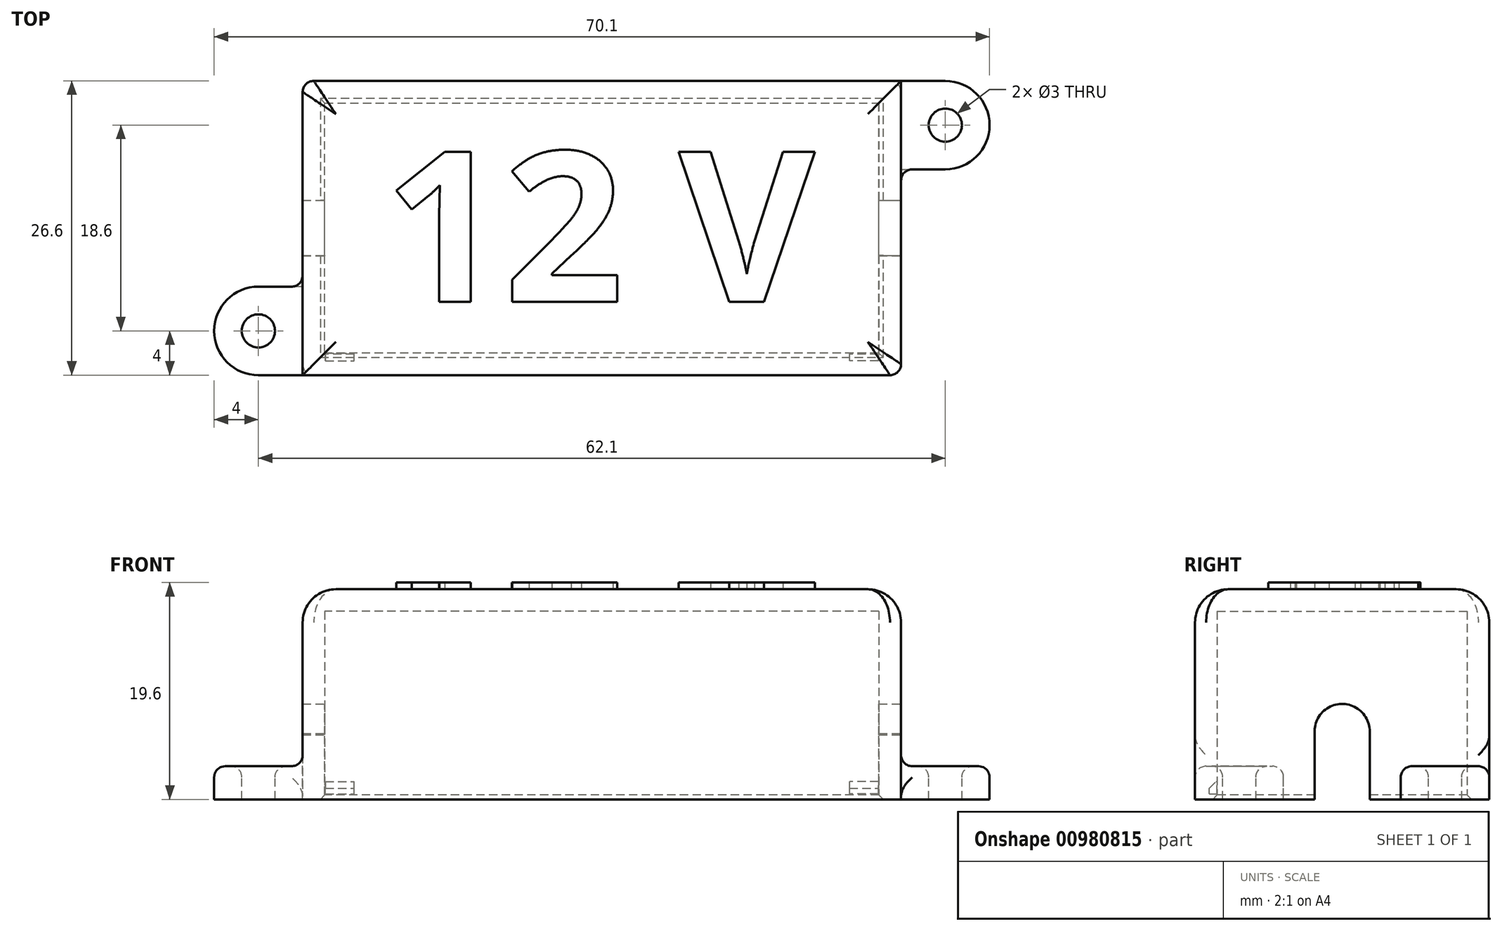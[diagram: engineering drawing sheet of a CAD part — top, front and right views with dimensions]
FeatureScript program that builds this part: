
annotation { "Feature Type Name" : "Feature", "Feature Type Description" : "" }
export const myFeature = defineFeature(function(context is Context, id is Id, definition is map)
    precondition{}
    {
        {
            var Q0;
            Q0=qCreatedBy(makeId("Top.planeOp"),FACE);
            var sketch = newSketch(context, id + "F0", { "sketchPlane" : qUnion([Q0])});
            skLineSegment(sketch, "E0.bottom", {"start": v(25.05, -11.3) * mm, "end": v(-25.05, -11.3) * mm});
            skLineSegment(sketch, "E0.top", {"start": v(25.05, 11.3) * mm, "end": v(-25.05, 11.3) * mm});
            skLineSegment(sketch, "E0.left", {"start": v(25.05, -11.3) * mm, "end": v(25.05, 11.3) * mm});
            skLineSegment(sketch, "E0.right", {"start": v(-25.05, -11.3) * mm, "end": v(-25.05, 11.3) * mm});
            skPoint(sketch, "E0.middle", {"position": v(0, 0) * mm});
            skLineSegment(sketch, "E1.bottom", {"start": v(27.05, -13.3) * mm, "end": v(-27.05, -13.3) * mm});
            skLineSegment(sketch, "E1.top", {"start": v(27.05, 13.3) * mm, "end": v(-27.05, 13.3) * mm});
            skLineSegment(sketch, "E1.left", {"start": v(27.05, -13.3) * mm, "end": v(27.05, 13.3) * mm});
            skLineSegment(sketch, "E1.right", {"start": v(-27.05, -13.3) * mm, "end": v(-27.05, 13.3) * mm});
            skSolve(sketch);
        }
        {
            var Q0;
            Q0 = qSketchRegion(id + "F0", true);
            extrude(context, id + "F1", {"entities" : qUnion([Q0]), "depth" : 17 * mm, "offsetDistance" : 25 * mm});
        }
        {
            var Q0;
            Q0=makeQuery(id+"F1.opExtrude","CAP_FACE",FACE,{"disambiguationData":[OSD([sQuery(id+"F0.wireOp",EDGE,"E0.bottom"),sQuery(id+"F0.wireOp",EDGE,"E0.top"),sQuery(id+"F0.wireOp",EDGE,"E0.left"),sQuery(id+"F0.wireOp",EDGE,"E0.right"),sQuery(id+"F0.wireOp",EDGE,"E1.bottom"),sQuery(id+"F0.wireOp",EDGE,"E1.top"),sQuery(id+"F0.wireOp",EDGE,"E1.left"),sQuery(id+"F0.wireOp",EDGE,"E1.right")])],"isStart":false});
            var sketch = newSketch(context, id + "F2", { "sketchPlane" : qUnion([Q0])});
            skLineSegment(sketch, "E2.0", {"start": v(-27.05, -13.3) * mm, "end": v(-27.05, 13.3) * mm});
            skLineSegment(sketch, "E3.0", {"start": v(27.05, 13.3) * mm, "end": v(-27.05, 13.3) * mm});
            skLineSegment(sketch, "E4.0", {"start": v(27.05, -13.3) * mm, "end": v(27.05, 13.3) * mm});
            skLineSegment(sketch, "E5.0", {"start": v(27.05, -13.3) * mm, "end": v(-27.05, -13.3) * mm});
            skSolve(sketch);
        }
        {
            var Q0;
            Q0 = qSketchRegion(id + "F2", true);
            extrude(context, id + "F3", {"entities" : qUnion([Q0]), "operationType" : NewBodyOperationType.ADD, "depth" : 2 * mm, "offsetDistance" : 25 * mm});
        }
        {
            var Q0;
            Q0=makeQuery(id+"F3.boolean.opBoolean","MERGE",FACE,{"derivedFrom":[makeQuery(id+"F1.opExtrude","SWEPT_FACE",FACE,{"disambiguationData":[OSD([sQuery(id+"F0.wireOp",EDGE,"E1.left")])]}),makeQuery(id+"F3.opExtrude","SWEPT_FACE",FACE,{"disambiguationData":[OSD([sQuery(id+"F2.wireOp",EDGE,"E4.0")])]})]});
            var sketch = newSketch(context, id + "F4", { "sketchPlane" : qUnion([Q0])});
            skLineSegment(sketch, "E6", {"start": v(-2.48, 5.83) * mm, "end": v(-2.48, 0) * mm});
            skLineSegment(sketch, "E7", {"start": v(2.5, 5.96) * mm, "end": v(2.5, 0) * mm});
            skLineSegment(sketch, "E8", {"start": v(2.5, 0) * mm, "end": v(-2.48, 0) * mm});
            skArc(sketch, "E9.trimOffspring", {"start": v(2.5, 5.96) * mm, "mid": v(-0.07, 8.63) * mm, "end": v(-2.48, 5.83) * mm});
            skLineSegment(sketch, "E10.trimOffspring", {"start": v(2.5, 3.63) * mm, "end": v(3.32, 3.63) * mm, "construction": true});
            skPoint(sketch, "E11.start.orphan", {"position": v(0, 3.63) * mm});
            skSolve(sketch);
        }
        {
            var Q0;
            Q0 = qSketchRegion(id + "F4", true);
            extrude(context, id + "F5", {"entities" : qUnion([Q0]), "operationType" : NewBodyOperationType.REMOVE, "endBound" : BoundingType.THROUGH_ALL, "oppositeDirection" : true, "depth" : 25 * mm, "offsetDistance" : 25 * mm});
        }
        {
            var Q0;
            Q0=makeQuery(id+"F3.boolean.opBoolean","MERGE",FACE,{"derivedFrom":[makeQuery(id+"F1.opExtrude","SWEPT_FACE",FACE,{"disambiguationData":[OSD([sQuery(id+"F0.wireOp",EDGE,"E1.left")])]}),makeQuery(id+"F3.opExtrude","SWEPT_FACE",FACE,{"disambiguationData":[OSD([sQuery(id+"F2.wireOp",EDGE,"E4.0")])]})]});
            var sketch = newSketch(context, id + "F6", { "sketchPlane" : qUnion([Q0])});
            skLineSegment(sketch, "E12.bottom", {"start": v(13.3, 0) * mm, "end": v(5.3, 0) * mm});
            skLineSegment(sketch, "E12.top", {"start": v(13.3, 3) * mm, "end": v(5.3, 3) * mm});
            skLineSegment(sketch, "E12.left", {"start": v(13.3, 0) * mm, "end": v(13.3, 3) * mm});
            skLineSegment(sketch, "E12.right", {"start": v(5.3, 0) * mm, "end": v(5.3, 3) * mm});
            skSolve(sketch);
        }
        {
            var Q0;
            Q0 = qSketchRegion(id + "F6", true);
            extrude(context, id + "F7", {"entities" : qUnion([Q0]), "operationType" : NewBodyOperationType.ADD, "depth" : 8 * mm, "offsetDistance" : 25 * mm});
        }
        {
            var Q0;
            Q0=makeQuery(id+"F7.opExtrude","CAP_EDGE",EDGE,{"disambiguationData":[OSD([sQuery(id+"F6.wireOp",EDGE,"E12.right")])],"isStart":false});
            var Q1;
            Q1=makeQuery(id+"F7.opExtrude","CAP_EDGE",EDGE,{"disambiguationData":[OSD([sQuery(id+"F6.wireOp",EDGE,"E12.left")])],"isStart":false});
            fillet(context, id + "F8", {"entities" : qUnion([Q0, Q1]), "radius" : 4 * mm, "tangentPropagation" : true, "allowEdgeOverflow" : false});
        }
        {
            var Q0;
            Q0=makeQuery(id+"F3.boolean.opBoolean","MERGE",FACE,{"derivedFrom":[makeQuery(id+"F1.opExtrude","SWEPT_FACE",FACE,{"disambiguationData":[OSD([sQuery(id+"F0.wireOp",EDGE,"E1.right")])]}),makeQuery(id+"F3.opExtrude","SWEPT_FACE",FACE,{"disambiguationData":[OSD([sQuery(id+"F2.wireOp",EDGE,"E2.0")])]})]});
            var sketch = newSketch(context, id + "F9", { "sketchPlane" : qUnion([Q0])});
            skLineSegment(sketch, "E13.bottom", {"start": v(13.3, 0) * mm, "end": v(5.3, 0) * mm});
            skLineSegment(sketch, "E13.top", {"start": v(13.3, 3) * mm, "end": v(5.3, 3) * mm});
            skLineSegment(sketch, "E13.left", {"start": v(13.3, 0) * mm, "end": v(13.3, 3) * mm});
            skLineSegment(sketch, "E13.right", {"start": v(5.3, 0) * mm, "end": v(5.3, 3) * mm});
            skSolve(sketch);
        }
        {
            var Q0;
            Q0 = qSketchRegion(id + "F9", true);
            extrude(context, id + "F10", {"entities" : qUnion([Q0]), "operationType" : NewBodyOperationType.ADD, "depth" : 8 * mm, "offsetDistance" : 25 * mm});
        }
        {
            var Q0;
            Q0=makeQuery(id+"F10.opExtrude","CAP_EDGE",EDGE,{"disambiguationData":[OSD([sQuery(id+"F9.wireOp",EDGE,"E13.right")])],"isStart":false});
            var Q1;
            Q1=makeQuery(id+"F10.opExtrude","CAP_EDGE",EDGE,{"disambiguationData":[OSD([sQuery(id+"F9.wireOp",EDGE,"E13.left")])],"isStart":false});
            fillet(context, id + "F11", {"entities" : qUnion([Q0, Q1]), "radius" : 4 * mm, "tangentPropagation" : true, "allowEdgeOverflow" : false});
        }
        {
            var Q0;
            Q0=makeQuery(id+"F10.opExtrude","SWEPT_FACE",FACE,{"disambiguationData":[OSD([sQuery(id+"F9.wireOp",EDGE,"E13.top")])]});
            var sketch = newSketch(context, id + "F12", { "sketchPlane" : qUnion([Q0])});
            skLineSegment(sketch, "E14", {"start": v(-31.05, -5.3) * mm, "end": v(-31.05, -13.3) * mm, "construction": true});
            skCircle(sketch, "E15", {"center": v(-31.05, -9.3) * mm, "radius": 1.5 * mm});
            skSolve(sketch);
        }
        {
            var Q0;
            Q0 = qSketchRegion(id + "F12", true);
            extrude(context, id + "F13", {"entities" : qUnion([Q0]), "operationType" : NewBodyOperationType.REMOVE, "oppositeDirection" : true, "depth" : 25 * mm, "offsetDistance" : 25 * mm});
        }
        {
            var Q0;
            Q0=makeQuery(id+"F7.opExtrude","SWEPT_FACE",FACE,{"disambiguationData":[OSD([sQuery(id+"F6.wireOp",EDGE,"E12.top")])]});
            var sketch = newSketch(context, id + "F14", { "sketchPlane" : qUnion([Q0])});
            skLineSegment(sketch, "E16", {"start": v(31.05, 13.3) * mm, "end": v(31.05, 5.3) * mm, "construction": true});
            skCircle(sketch, "E17", {"center": v(31.05, 9.3) * mm, "radius": 1.5 * mm});
            skSolve(sketch);
        }
        {
            var Q0;
            Q0 = qSketchRegion(id + "F14", true);
            extrude(context, id + "F15", {"entities" : qUnion([Q0]), "operationType" : NewBodyOperationType.REMOVE, "oppositeDirection" : true, "depth" : 25 * mm, "offsetDistance" : 25 * mm});
        }
        {
            var Q0;
            Q0=makeQuery(id+"F3.opExtrude","CAP_FACE",FACE,{"disambiguationData":[OSD([sQuery(id+"F2.wireOp",EDGE,"E2.0"),sQuery(id+"F2.wireOp",EDGE,"E3.0"),sQuery(id+"F2.wireOp",EDGE,"E4.0"),sQuery(id+"F2.wireOp",EDGE,"E5.0")])],"isStart":false});
            fillet(context, id + "F16", {"entities" : qUnion([Q0]), "radius" : 3 * mm, "tangentPropagation" : true, "allowEdgeOverflow" : false});
        }
        {
            var Q0;
            Q0=makeQuery(id+"F1.opExtrude","SWEPT_FACE",FACE,{"disambiguationData":[OSD([sQuery(id+"F0.wireOp",EDGE,"E0.bottom")])]});
            var sketch = newSketch(context, id + "F17", { "sketchPlane" : qUnion([Q0])});
            skLineSegment(sketch, "E18", {"start": v(0, 0) * mm, "end": v(0, 17) * mm, "construction": true});
            skLineSegment(sketch, "E19.bottom", {"start": v(25, 0.5) * mm, "end": v(22.4, 0.5) * mm});
            skLineSegment(sketch, "E19.top", {"start": v(25, 1.6) * mm, "end": v(22.4, 1.6) * mm});
            skLineSegment(sketch, "E19.left", {"start": v(25, 0.5) * mm, "end": v(25, 1.6) * mm});
            skLineSegment(sketch, "E19.right", {"start": v(22.4, 0.5) * mm, "end": v(22.4, 1.6) * mm});
            skLineSegment(sketch, "E20.MirrorCS", {"start": v(-25, 1.6) * mm, "end": v(-22.4, 1.6) * mm});
            skLineSegment(sketch, "E21.MirrorCS", {"start": v(-25, 0.5) * mm, "end": v(-22.4, 0.5) * mm});
            skLineSegment(sketch, "E22.MirrorCS", {"start": v(-22.4, 0.5) * mm, "end": v(-22.4, 1.6) * mm});
            skLineSegment(sketch, "E23.MirrorCS", {"start": v(-25, 0.5) * mm, "end": v(-25, 1.6) * mm});
            skSolve(sketch);
        }
        {
            var Q0;
            Q0 = qSketchRegion(id + "F17", true);
            extrude(context, id + "F18", {"entities" : qUnion([Q0]), "operationType" : NewBodyOperationType.REMOVE, "oppositeDirection" : true, "depth" : .7 * mm, "offsetDistance" : 25 * mm});
        }
        {
            var Q0;
            Q0=makeQuery(id+"F18.boolean.opBoolean","COPY",EDGE,{"derivedFrom":makeQuery(id+"F18.opExtrude","CAP_EDGE",EDGE,{"disambiguationData":[OSD([sQuery(id+"F17.wireOp",EDGE,"E20.MirrorCS")])],"isStart":false})});
            var Q1;
            Q1=makeQuery(id+"F18.boolean.opBoolean","COPY",EDGE,{"derivedFrom":makeQuery(id+"F18.opExtrude","CAP_EDGE",EDGE,{"disambiguationData":[OSD([sQuery(id+"F17.wireOp",EDGE,"E19.top")])],"isStart":false})});
            chamfer(context, id + "F19", {"entities" : qUnion([Q0, Q1]), "width" : .6 * mm, "tangentPropagation" : true});
        }
        {
            var Q0;
            Q0=makeQuery(id+"F10.opExtrude","SWEPT_FACE",FACE,{"disambiguationData":[OSD([sQuery(id+"F9.wireOp",EDGE,"E13.top")])]});
            var Q1;
            Q1=makeQuery(id+"F7.opExtrude","SWEPT_FACE",FACE,{"disambiguationData":[OSD([sQuery(id+"F6.wireOp",EDGE,"E12.top")])]});
            var Q2;
            Q2=makeQuery(id+"F3.boolean.opBoolean","MERGE",EDGE,{"derivedFrom":[makeQuery(id+"F1.opExtrude","SWEPT_EDGE",EDGE,{"disambiguationData":[OSD([sQuery(id+"F0.wireOp",EDGE,"E1.bottom"),sQuery(id+"F0.wireOp",EDGE,"E1.left")])]}),makeQuery(id+"F3.opExtrude","SWEPT_EDGE",EDGE,{"disambiguationData":[OSD([sQuery(id+"F2.wireOp",EDGE,"E4.0"),sQuery(id+"F2.wireOp",EDGE,"E5.0")])]})]});
            var Q3;
            Q3=makeQuery(id+"F3.boolean.opBoolean","MERGE",EDGE,{"derivedFrom":[makeQuery(id+"F1.opExtrude","SWEPT_EDGE",EDGE,{"disambiguationData":[OSD([sQuery(id+"F0.wireOp",EDGE,"E1.top"),sQuery(id+"F0.wireOp",EDGE,"E1.right")])]}),makeQuery(id+"F3.opExtrude","SWEPT_EDGE",EDGE,{"disambiguationData":[OSD([sQuery(id+"F2.wireOp",EDGE,"E2.0"),sQuery(id+"F2.wireOp",EDGE,"E3.0")])]})]});
            fillet(context, id + "F20", {"entities" : qUnion([Q0, Q1, Q2, Q3]), "tangentPropagation" : true, "radius" : 1 * mm, "defaultsChanged" : false, "vertexSettings" : [], "allowEdgeOverflow" : false});
        }
        {
            var Q0;
            Q0=makeQuery(id+"F3.opExtrude","CAP_FACE",FACE,{"disambiguationData":[OSD([sQuery(id+"F2.wireOp",EDGE,"E2.0"),sQuery(id+"F2.wireOp",EDGE,"E3.0"),sQuery(id+"F2.wireOp",EDGE,"E4.0"),sQuery(id+"F2.wireOp",EDGE,"E5.0")])],"isStart":false});
            var sketch = newSketch(context, id + "F21", { "sketchPlane" : qUnion([Q0])});
            skText(sketch, "E24", { "text": "12 V", "fontName": "OpenSans-Bold.ttf"});
            const initialGuessF21  = {"E24": [-0.0197, -0.00668, 1, 0, 0.01368]};
            skSetInitialGuess(sketch, initialGuessF21);
            skSolve(sketch);
        }
        {
            var Q0;
            Q0 = qSketchRegion(id + "F21", true);
            extrude(context, id + "F22", {"entities" : qUnion([Q0]), "operationType" : NewBodyOperationType.ADD, "depth" : .6 * mm, "offsetDistance" : 25 * mm});
        }
        {
            var Q0;
            Q0=makeQuery(id+"F1.opExtrude","CAP_EDGE",EDGE,{"disambiguationData":[OSD([sQuery(id+"F0.wireOp",EDGE,"E0.bottom")])],"isStart":true});
            var Q1;
            {var subQ0=sQuery(id+"F0.wireOp",EDGE,"E0.bottom");var subQ1=sQuery(id+"F0.wireOp",EDGE,"E0.right");Q1=makeQuery(id+"F5.boolean.opBoolean","SPLIT",EDGE,{"disambiguationData":[TD([makeQuery(id+"F1.opExtrude","SWEPT_FACE",FACE,{"disambiguationData":[OSD([subQ0])]})])],"derivedFrom":makeQuery(id+"F1.opExtrude","CAP_EDGE",EDGE,{"disambiguationData":[OSD([subQ1])],"isStart":true})});}
            var Q2;
            {var subQ1=sQuery(id+"F0.wireOp",EDGE,"E1.left");var subQ2=sQuery(id+"F0.wireOp",EDGE,"E0.right");var subQ3=sQuery(id+"F4.wireOp",EDGE,"E6");Q2=makeQuery(id+"F5.boolean.opBoolean","COPY",EDGE,{"disambiguationData":[TD([makeQuery(id+"F1.opExtrude","SWEPT_FACE",FACE,{"disambiguationData":[OSD([subQ2])]})])],"derivedFrom":makeQuery(id+"F5.opExtrude","SWEPT_EDGE",EDGE,{"disambiguationData":[OSD([subQ1,subQ3,sQuery(id+"F4.wireOp",EDGE,"E8")])]})});}
            var Q3;
            {var subQ1=sQuery(id+"F0.wireOp",EDGE,"E1.left");var subQ2=sQuery(id+"F0.wireOp",EDGE,"E0.right");var subQ3=sQuery(id+"F4.wireOp",EDGE,"E7");Q3=makeQuery(id+"F5.boolean.opBoolean","COPY",EDGE,{"disambiguationData":[TD([makeQuery(id+"F1.opExtrude","SWEPT_FACE",FACE,{"disambiguationData":[OSD([subQ2])]})])],"derivedFrom":makeQuery(id+"F5.opExtrude","SWEPT_EDGE",EDGE,{"disambiguationData":[OSD([subQ1,subQ3,sQuery(id+"F4.wireOp",EDGE,"E8")])]})});}
            var Q4;
            {var subQ0=sQuery(id+"F0.wireOp",EDGE,"E0.right");var subQ1=sQuery(id+"F0.wireOp",EDGE,"E0.top");Q4=makeQuery(id+"F5.boolean.opBoolean","SPLIT",EDGE,{"disambiguationData":[TD([makeQuery(id+"F1.opExtrude","SWEPT_FACE",FACE,{"disambiguationData":[OSD([subQ1])]})])],"derivedFrom":makeQuery(id+"F1.opExtrude","CAP_EDGE",EDGE,{"disambiguationData":[OSD([subQ0])],"isStart":true})});}
            var Q5;
            Q5=makeQuery(id+"F1.opExtrude","CAP_EDGE",EDGE,{"disambiguationData":[OSD([sQuery(id+"F0.wireOp",EDGE,"E0.top")])],"isStart":true});
            var Q6;
            {var subQ0=sQuery(id+"F0.wireOp",EDGE,"E0.left");var subQ1=sQuery(id+"F0.wireOp",EDGE,"E0.top");Q6=makeQuery(id+"F5.boolean.opBoolean","SPLIT",EDGE,{"disambiguationData":[TD([makeQuery(id+"F1.opExtrude","SWEPT_FACE",FACE,{"disambiguationData":[OSD([subQ1])]})])],"derivedFrom":makeQuery(id+"F1.opExtrude","CAP_EDGE",EDGE,{"disambiguationData":[OSD([subQ0])],"isStart":true})});}
            var Q7;
            {var subQ0=sQuery(id+"F0.wireOp",EDGE,"E1.left");var subQ1=sQuery(id+"F0.wireOp",EDGE,"E0.left");var subQ2=sQuery(id+"F4.wireOp",EDGE,"E6");Q7=makeQuery(id+"F5.boolean.opBoolean","COPY",EDGE,{"disambiguationData":[TD([makeQuery(id+"F1.opExtrude","SWEPT_FACE",FACE,{"disambiguationData":[OSD([subQ1])]})])],"derivedFrom":makeQuery(id+"F5.opExtrude","SWEPT_EDGE",EDGE,{"disambiguationData":[OSD([subQ0,subQ2,sQuery(id+"F4.wireOp",EDGE,"E8")])]})});}
            var Q8;
            {var subQ0=sQuery(id+"F0.wireOp",EDGE,"E1.left");var subQ1=sQuery(id+"F0.wireOp",EDGE,"E0.left");var subQ2=sQuery(id+"F4.wireOp",EDGE,"E7");Q8=makeQuery(id+"F5.boolean.opBoolean","COPY",EDGE,{"disambiguationData":[TD([makeQuery(id+"F1.opExtrude","SWEPT_FACE",FACE,{"disambiguationData":[OSD([subQ1])]})])],"derivedFrom":makeQuery(id+"F5.opExtrude","SWEPT_EDGE",EDGE,{"disambiguationData":[OSD([subQ0,subQ2,sQuery(id+"F4.wireOp",EDGE,"E8")])]})});}
            var Q9;
            {var subQ0=sQuery(id+"F0.wireOp",EDGE,"E0.bottom");var subQ1=sQuery(id+"F0.wireOp",EDGE,"E0.left");Q9=makeQuery(id+"F5.boolean.opBoolean","SPLIT",EDGE,{"disambiguationData":[TD([makeQuery(id+"F1.opExtrude","SWEPT_FACE",FACE,{"disambiguationData":[OSD([subQ0])]})])],"derivedFrom":makeQuery(id+"F1.opExtrude","CAP_EDGE",EDGE,{"disambiguationData":[OSD([subQ1])],"isStart":true})});}
            chamfer(context, id + "F23", {"entities" : qUnion([Q0, Q1, Q2, Q3, Q4, Q5, Q6, Q7, Q8, Q9]), "width" : .4 * mm, "tangentPropagation" : true});
        }
    });
